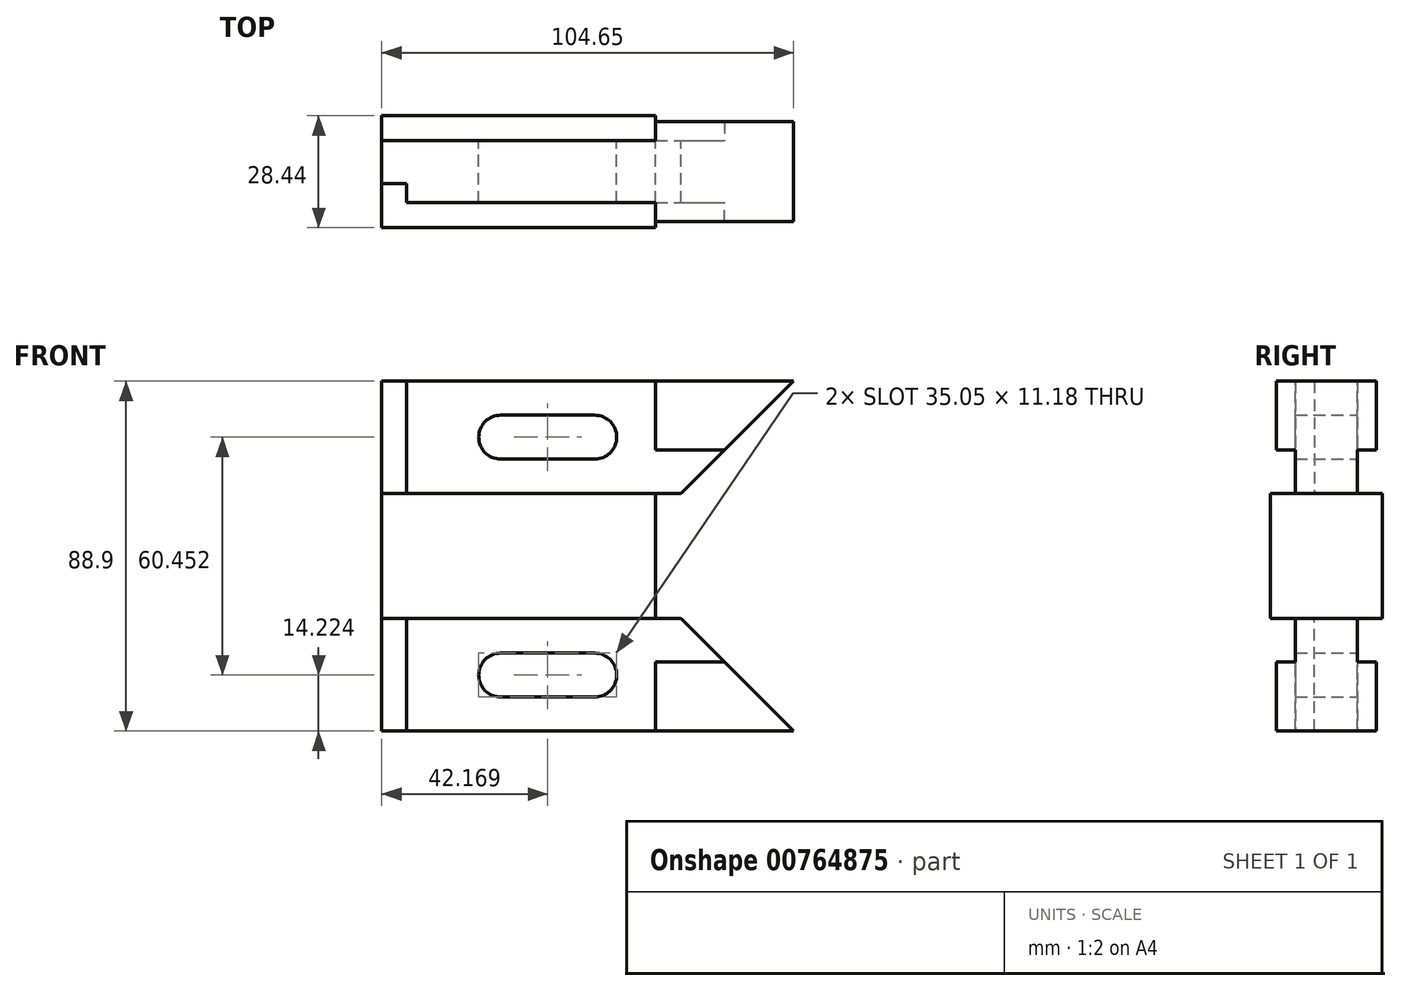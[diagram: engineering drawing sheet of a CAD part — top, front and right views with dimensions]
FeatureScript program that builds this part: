
annotation { "Feature Type Name" : "Feature", "Feature Type Description" : "" }
export const myFeature = defineFeature(function(context is Context, id is Id, definition is map)
    precondition{}
    {
        {
            var Q0;
            Q0=qCreatedBy(makeId("Front.planeOp"),FACE);
            var sketch = newSketch(context, id + "F0", { "sketchPlane" : qUnion([Q0])});
            skLineSegment(sketch, "E0", {"start": v(-44.34, 0) * mm, "end": v(-44.34, 44.45) * mm});
            skLineSegment(sketch, "E1", {"start": v(-44.34, 44.45) * mm, "end": v(60.31, 44.45) * mm});
            skLineSegment(sketch, "E2", {"start": v(31.74, 15.88) * mm, "end": v(60.31, 44.45) * mm});
            skLineSegment(sketch, "E3", {"start": v(-44.34, 15.88) * mm, "end": v(25.26, 15.88) * mm});
            skLineSegment(sketch, "E4", {"start": v(25.26, 15.88) * mm, "end": v(25.26, 0) * mm});
            skLineSegment(sketch, "E5", {"start": v(25.26, 15.88) * mm, "end": v(31.74, 15.88) * mm});
            skLineSegment(sketch, "E6", {"start": v(-19.7, 35.81) * mm, "end": v(15.35, 35.81) * mm});
            skLineSegment(sketch, "E7", {"start": v(15.35, 24.64) * mm, "end": v(-19.7, 24.64) * mm});
            skLineSegment(sketch, "E8", {"start": v(15.35, 30.23) * mm, "end": v(9.77, 30.23) * mm});
            skLineSegment(sketch, "E9", {"start": v(-19.7, 30.23) * mm, "end": v(-14.1, 30.23) * mm});
            skCircle(sketch, "E10", {"center": v(-14.1, 30.23) * mm, "radius": 5.59 * mm});
            skCircle(sketch, "E11", {"center": v(9.77, 30.23) * mm, "radius": 5.59 * mm});
            skLineSegment(sketch, "E12.MirrorCS", {"start": v(25.26, -15.88) * mm, "end": v(31.74, -15.88) * mm});
            skLineSegment(sketch, "E13.MirrorCS", {"start": v(15.35, -30.23) * mm, "end": v(9.77, -30.23) * mm});
            skLineSegment(sketch, "E14.MirrorCS", {"start": v(-19.7, -30.23) * mm, "end": v(-14.1, -30.23) * mm});
            skLineSegment(sketch, "E15.MirrorCS", {"start": v(-44.34, 0) * mm, "end": v(-44.34, -44.45) * mm});
            skLineSegment(sketch, "E16.MirrorCS", {"start": v(-44.34, -44.45) * mm, "end": v(60.31, -44.45) * mm});
            skLineSegment(sketch, "E17.MirrorCS", {"start": v(31.74, -15.88) * mm, "end": v(60.31, -44.45) * mm});
            skCircle(sketch, "E18.MirrorC", {"center": v(9.77, -30.23) * mm, "radius": 5.59 * mm});
            skLineSegment(sketch, "E19.MirrorCS", {"start": v(25.26, -15.88) * mm, "end": v(25.26, 0) * mm});
            skLineSegment(sketch, "E20.MirrorCS", {"start": v(-19.7, -35.81) * mm, "end": v(15.35, -35.81) * mm});
            skCircle(sketch, "E21.MirrorC", {"center": v(-14.1, -30.23) * mm, "radius": 5.59 * mm});
            skLineSegment(sketch, "E22.MirrorCS", {"start": v(15.35, -24.64) * mm, "end": v(-19.7, -24.64) * mm});
            skLineSegment(sketch, "E23.MirrorCS", {"start": v(-44.34, -15.88) * mm, "end": v(25.26, -15.88) * mm});
            skSolve(sketch);
        }
        {
            var Q0;
            {var subQ4=sQuery(id+"F0.wireOp",EDGE,"E3");Q0=makeQuery(id+"F0.imprint","IMPRINT",FACE,{"disambiguationData":[TD([[makeQuery(id+"F0.imprint","IMPRINT",EDGE,{"derivedFrom":subQ4}),-1.0]])]});}
            extrude(context, id + "F1", {"entities" : qUnion([Q0]), "depth" : 28.45 * mm, "offsetDistance" : 25.4 * mm, "symmetric" : true});
        }
        {
            var Q0;
            Q0=makeQuery(id+"F0.imprint","IMPRINT",FACE,{"disambiguationData":[TD([[makeQuery(id+"F0.imprint","IMPRINT",EDGE,{"derivedFrom":sQuery(id+"F0.wireOp",EDGE,"E12.MirrorCS")}),-1.0]])]});
            extrude(context, id + "F2", {"entities" : qUnion([Q0]), "operationType" : NewBodyOperationType.ADD, "depth" : 15.75 * mm, "offsetDistance" : 25.4 * mm, "symmetric" : true});
        }
        {
            var Q0;
            {var subQ10=sQuery(id+"F0.wireOp",EDGE,"E1");Q0=makeQuery(id+"F0.imprint","IMPRINT",FACE,{"disambiguationData":[TD([[makeQuery(id+"F0.imprint","IMPRINT",EDGE,{"derivedFrom":subQ10}),-1.0]])]});}
            extrude(context, id + "F3", {"entities" : qUnion([Q0]), "operationType" : NewBodyOperationType.ADD, "depth" : 15.75 * mm, "offsetDistance" : 25.4 * mm, "symmetric" : true});
        }
        {
            var Q0;
            Q0=makeQuery(id+"F3.opExtrude","CAP_FACE",FACE,{"disambiguationData":[OSD([sQuery(id+"F0.wireOp",EDGE,"E0"),sQuery(id+"F0.wireOp",EDGE,"E1"),sQuery(id+"F0.wireOp",EDGE,"E2"),sQuery(id+"F0.wireOp",EDGE,"E3"),sQuery(id+"F0.wireOp",EDGE,"E5"),sQuery(id+"F0.wireOp",EDGE,"E6"),sQuery(id+"F0.wireOp",EDGE,"E7"),sQuery(id+"F0.wireOp",EDGE,"E10"),sQuery(id+"F0.wireOp",EDGE,"E11")])],"isStart":false});
            var sketch = newSketch(context, id + "F4", { "sketchPlane" : qUnion([Q0])});
            skLineSegment(sketch, "E24", {"start": v(-44.34, 44.45) * mm, "end": v(25.26, 44.45) * mm});
            skLineSegment(sketch, "E25", {"start": v(25.26, 44.45) * mm, "end": v(25.26, 26.92) * mm});
            skLineSegment(sketch, "E26", {"start": v(25.26, 26.92) * mm, "end": v(42.79, 26.92) * mm});
            skLineSegment(sketch, "E27", {"start": v(42.79, 26.92) * mm, "end": v(60.31, 44.45) * mm});
            skLineSegment(sketch, "E28", {"start": v(60.31, 44.45) * mm, "end": v(25.26, 44.45) * mm});
            skLineSegment(sketch, "E29.MirrorCS", {"start": v(60.31, -44.45) * mm, "end": v(25.26, -44.45) * mm});
            skLineSegment(sketch, "E30.MirrorCS", {"start": v(25.26, -26.92) * mm, "end": v(42.79, -26.92) * mm});
            skLineSegment(sketch, "E31.MirrorCS", {"start": v(25.26, -44.45) * mm, "end": v(25.26, -26.92) * mm});
            skLineSegment(sketch, "E32.MirrorCS", {"start": v(42.79, -26.92) * mm, "end": v(60.31, -44.45) * mm});
            skSolve(sketch);
        }
        {
            var Q0;
            Q0=makeQuery(id+"F4.imprint","IMPRINT",FACE,{"disambiguationData":[TD([[makeQuery(id+"F4.imprint","IMPRINT",EDGE,{"derivedFrom":sQuery(id+"F4.wireOp",EDGE,"E25")}),1.0]])]});
            var Q1;
            Q1=makeQuery(id+"F4.imprint","IMPRINT",FACE,{"disambiguationData":[TD([[makeQuery(id+"F4.imprint","IMPRINT",EDGE,{"derivedFrom":sQuery(id+"F4.wireOp",EDGE,"E29.MirrorCS")}),-1.0]])]});
            extrude(context, id + "F5", {"entities" : qUnion([Q0, Q1]), "operationType" : NewBodyOperationType.ADD, "depth" : 4.83 * mm, "offsetDistance" : 25.4 * mm});
        }
        {
            var Q0;
            Q0=makeQuery(id+"F5.opExtrude","CAP_FACE",FACE,{"disambiguationData":[OSD([sQuery(id+"F4.wireOp",EDGE,"E25"),sQuery(id+"F4.wireOp",EDGE,"E26"),sQuery(id+"F4.wireOp",EDGE,"E27"),sQuery(id+"F4.wireOp",EDGE,"E28")])],"isStart":false});
            var Q1;
            Q1=makeQuery(id+"F5.opExtrude","CAP_FACE",FACE,{"disambiguationData":[OSD([sQuery(id+"F4.wireOp",EDGE,"E29.MirrorCS"),sQuery(id+"F4.wireOp",EDGE,"E30.MirrorCS"),sQuery(id+"F4.wireOp",EDGE,"E31.MirrorCS"),sQuery(id+"F4.wireOp",EDGE,"E32.MirrorCS")])],"isStart":false});
            extrude(context, id + "F6", {"entities" : qUnion([Q0, Q1]), "operationType" : NewBodyOperationType.ADD, "oppositeDirection" : true, "depth" : 25.4 * mm, "offsetDistance" : 25.4 * mm});
        }
        {
            var Q0;
            {var subQ0=sQuery(id+"F0.wireOp",EDGE,"E0");var subQ1=sQuery(id+"F0.wireOp",EDGE,"E15.MirrorCS");Q0=makeQuery(id+"F3.boolean.opBoolean","MERGE",FACE,{"derivedFrom":[makeQuery(id+"F2.boolean.opBoolean","MERGE",FACE,{"derivedFrom":[makeQuery(id+"F1.opExtrude","SWEPT_FACE",FACE,{"disambiguationData":[OSD([subQ0,subQ1])]}),makeQuery(id+"F2.opExtrude","SWEPT_FACE",FACE,{"disambiguationData":[OSD([subQ1])]})]}),makeQuery(id+"F3.opExtrude","SWEPT_FACE",FACE,{"disambiguationData":[OSD([subQ0])]})]});}
            var sketch = newSketch(context, id + "F7", { "sketchPlane" : qUnion([Q0])});
            skLineSegment(sketch, "E33", {"start": v(7.87, 44.45) * mm, "end": v(3.05, 44.45) * mm});
            skLineSegment(sketch, "E34", {"start": v(3.05, 44.45) * mm, "end": v(3.05, 15.88) * mm});
            skLineSegment(sketch, "E35", {"start": v(3.05, 15.88) * mm, "end": v(7.87, 15.88) * mm});
            skLineSegment(sketch, "E36", {"start": v(7.87, 15.88) * mm, "end": v(7.87, 44.45) * mm});
            skLineSegment(sketch, "E37.MirrorCS", {"start": v(7.87, -44.45) * mm, "end": v(3.05, -44.45) * mm});
            skLineSegment(sketch, "E38.MirrorCS", {"start": v(3.05, -15.88) * mm, "end": v(7.87, -15.88) * mm});
            skLineSegment(sketch, "E39.MirrorCS", {"start": v(7.87, -15.88) * mm, "end": v(7.87, -44.45) * mm});
            skLineSegment(sketch, "E40.MirrorCS", {"start": v(3.05, -44.45) * mm, "end": v(3.05, -15.88) * mm});
            skSolve(sketch);
        }
        {
            var Q0;
            Q0=makeQuery(id+"F7.imprint","IMPRINT",FACE,{"disambiguationData":[TD([[makeQuery(id+"F7.imprint","IMPRINT",EDGE,{"derivedFrom":sQuery(id+"F7.wireOp",EDGE,"E33")}),1.0]])]});
            var Q1;
            Q1=makeQuery(id+"F7.imprint","IMPRINT",FACE,{"disambiguationData":[TD([[makeQuery(id+"F7.imprint","IMPRINT",EDGE,{"derivedFrom":sQuery(id+"F7.wireOp",EDGE,"E37.MirrorCS")}),-1.0]])]});
            extrude(context, id + "F8", {"entities" : qUnion([Q0, Q1]), "operationType" : NewBodyOperationType.REMOVE, "oppositeDirection" : true, "depth" : 6.35 * mm, "offsetDistance" : 25.4 * mm});
        }
    });
